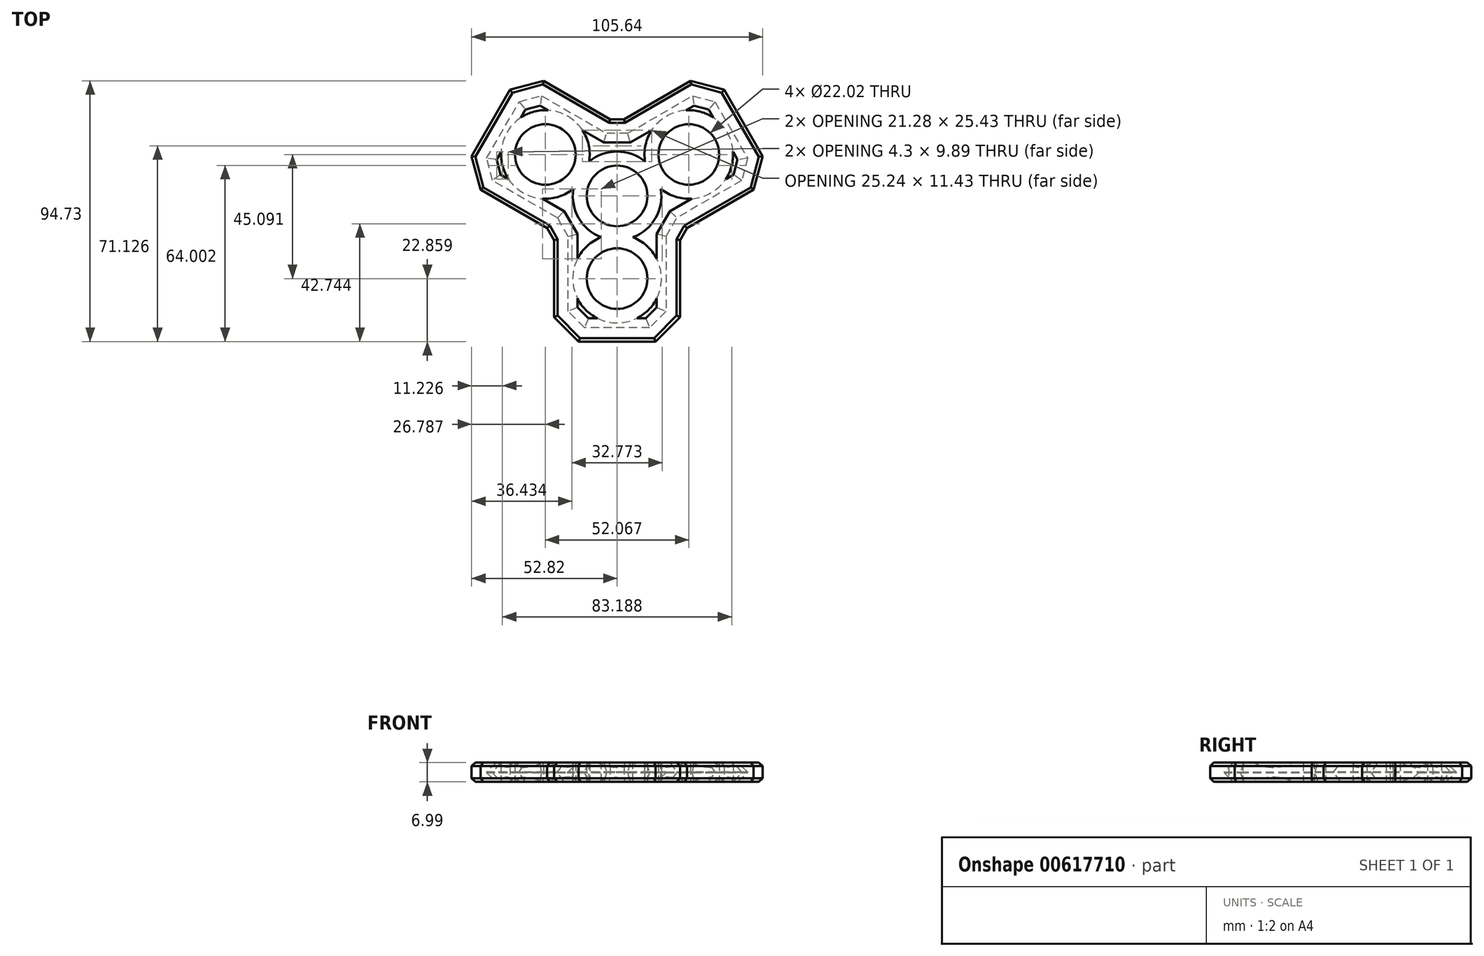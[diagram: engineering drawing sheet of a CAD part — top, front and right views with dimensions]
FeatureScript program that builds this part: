
annotation { "Feature Type Name" : "Feature", "Feature Type Description" : "" }
export const myFeature = defineFeature(function(context is Context, id is Id, definition is map)
    precondition{}
    {
        {
            var Q0;
            Q0=qCreatedBy(makeId("Top.planeOp"),FACE);
            var sketch = newSketch(context, id + "F0", { "sketchPlane" : qUnion([Q0])});
            skCircle(sketch, "E0", {"center": v(0, 0) * mm, "radius": 11.01 * mm});
            skCircle(sketch, "E1", {"center": v(0, 0) * mm, "radius": 19.05 * mm});
            skCircle(sketch, "E2", {"center": v(0, -30.06) * mm, "radius": 11.01 * mm});
            skLineSegment(sketch, "E3", {"start": v(0, 0) * mm, "end": v(0, -30.06) * mm});
            skCircle(sketch, "E4", {"center": v(0, -30.06) * mm, "radius": 19.05 * mm});
            skLineSegment(sketch, "E5", {"start": v(0, 0) * mm, "end": v(26.03, 15.03) * mm});
            skLineSegment(sketch, "E6", {"start": v(0, 0) * mm, "end": v(-26.03, 15.03) * mm});
            skCircle(sketch, "E7", {"center": v(-26.03, 15.03) * mm, "radius": 19.05 * mm});
            skCircle(sketch, "E8", {"center": v(26.03, 15.03) * mm, "radius": 19.05 * mm});
            skCircle(sketch, "E9", {"center": v(-26.03, 15.03) * mm, "radius": 11.01 * mm});
            skCircle(sketch, "E10", {"center": v(26.03, 15.03) * mm, "radius": 11.01 * mm});
            skLineSegment(sketch, "E11", {"start": v(-13.97, -52.92) * mm, "end": v(13.97, -52.92) * mm});
            skLineSegment(sketch, "E12", {"start": v(-22.86, -16.1) * mm, "end": v(-22.86, -44.03) * mm});
            skLineSegment(sketch, "E13", {"start": v(-22.86, -44.03) * mm, "end": v(-13.97, -52.92) * mm});
            skLineSegment(sketch, "E14", {"start": v(13.97, -52.92) * mm, "end": v(22.86, -44.03) * mm});
            skLineSegment(sketch, "E15", {"start": v(22.86, -44.03) * mm, "end": v(22.86, -16.1) * mm});
            skLineSegment(sketch, "E16", {"start": v(0, -30.06) * mm, "end": v(0, -52.92) * mm});
            skLineSegment(sketch, "E17", {"start": v(0, -30.06) * mm, "end": v(-22.86, -30.06) * mm});
            skLineSegment(sketch, "E18", {"start": v(0, -30.06) * mm, "end": v(22.86, -30.06) * mm});
            skLineSegment(sketch, "E19", {"start": v(18.42, -48.48) * mm, "end": v(0, -30.06) * mm});
            skLineSegment(sketch, "E20", {"start": v(-18.42, -48.48) * mm, "end": v(0, -30.06) * mm});
            skLineSegment(sketch, "E21.1.0", {"start": v(26.03, 15.03) * mm, "end": v(14.6, 34.83) * mm});
            skLineSegment(sketch, "E21.1.1", {"start": v(26.03, 15.03) * mm, "end": v(37.46, -4.77) * mm});
            skLineSegment(sketch, "E21.1.2", {"start": v(26.03, 15.03) * mm, "end": v(45.83, 26.46) * mm});
            skLineSegment(sketch, "E21.1.3", {"start": v(26.7, 41.81) * mm, "end": v(2.5, 27.84) * mm});
            skLineSegment(sketch, "E21.1.4", {"start": v(25.37, -11.75) * mm, "end": v(49.56, 2.22) * mm});
            skLineSegment(sketch, "E21.1.5", {"start": v(52.82, 14.36) * mm, "end": v(38.85, 38.56) * mm});
            skLineSegment(sketch, "E21.1.6", {"start": v(51.19, 8.3) * mm, "end": v(26.03, 15.03) * mm});
            skLineSegment(sketch, "E21.1.7", {"start": v(32.77, 40.19) * mm, "end": v(26.03, 15.03) * mm});
            skLineSegment(sketch, "E21.1.8", {"start": v(38.85, 38.56) * mm, "end": v(26.7, 41.81) * mm});
            skLineSegment(sketch, "E21.1.9", {"start": v(49.56, 2.22) * mm, "end": v(52.82, 14.36) * mm});
            skLineSegment(sketch, "E21.2.0", {"start": v(-26.03, 15.03) * mm, "end": v(-37.46, -4.77) * mm});
            skLineSegment(sketch, "E21.2.1", {"start": v(-26.03, 15.03) * mm, "end": v(-14.6, 34.83) * mm});
            skLineSegment(sketch, "E21.2.2", {"start": v(-26.03, 15.03) * mm, "end": v(-45.83, 26.46) * mm});
            skLineSegment(sketch, "E21.2.3", {"start": v(-49.56, 2.22) * mm, "end": v(-25.37, -11.75) * mm});
            skLineSegment(sketch, "E21.2.4", {"start": v(-2.5, 27.84) * mm, "end": v(-26.7, 41.81) * mm});
            skLineSegment(sketch, "E21.2.5", {"start": v(-38.85, 38.56) * mm, "end": v(-52.82, 14.36) * mm});
            skLineSegment(sketch, "E21.2.6", {"start": v(-32.77, 40.19) * mm, "end": v(-26.03, 15.03) * mm});
            skLineSegment(sketch, "E21.2.7", {"start": v(-51.19, 8.3) * mm, "end": v(-26.03, 15.03) * mm});
            skLineSegment(sketch, "E21.2.8", {"start": v(-52.82, 14.36) * mm, "end": v(-49.56, 2.22) * mm});
            skLineSegment(sketch, "E21.2.9", {"start": v(-26.7, 41.81) * mm, "end": v(-38.85, 38.56) * mm});
            skLineSegment(sketch, "E22", {"start": v(-22.86, -16.1) * mm, "end": v(-25.37, -11.75) * mm});
            skLineSegment(sketch, "E23", {"start": v(-2.5, 27.84) * mm, "end": v(2.5, 27.84) * mm});
            skLineSegment(sketch, "E24", {"start": v(25.37, -11.75) * mm, "end": v(22.86, -16.1) * mm});
            skSolve(sketch);
        }
        {
            var Q0;
            Q0 = qSketchRegion(id + "F0", true);
            var Q1;
            {var subQ0=sQuery(id+"F0.wireOp",EDGE,"E21.2.1");var subQ1=sQuery(id+"F0.wireOp",EDGE,"E7");var subQ2=makeQuery(id+"F0.imprint","INTERSECT",VERTEX,{"derivedFrom":[subQ1,subQ0]});Q1=makeQuery(id+"F0.imprint","IMPRINT",FACE,{"disambiguationData":[TD([[makeQuery(id+"F0.imprint","IMPRINT",EDGE,{"disambiguationData":[TD([[subQ2,-1.0]])],"derivedFrom":subQ1}),1.0]])]});}
            var Q2;
            {var subQ0=sQuery(id+"F0.wireOp",EDGE,"E21.2.6");var subQ1=sQuery(id+"F0.wireOp",EDGE,"E7");var subQ2=makeQuery(id+"F0.imprint","INTERSECT",VERTEX,{"derivedFrom":[subQ1,subQ0]});Q2=makeQuery(id+"F0.imprint","IMPRINT",FACE,{"disambiguationData":[TD([[makeQuery(id+"F0.imprint","IMPRINT",EDGE,{"disambiguationData":[TD([[subQ2,-1.0]])],"derivedFrom":subQ1}),1.0]])]});}
            var Q3;
            {var subQ0=sQuery(id+"F0.wireOp",EDGE,"E21.2.2");var subQ1=sQuery(id+"F0.wireOp",EDGE,"E7");var subQ2=makeQuery(id+"F0.imprint","INTERSECT",VERTEX,{"derivedFrom":[subQ1,subQ0]});Q3=makeQuery(id+"F0.imprint","IMPRINT",FACE,{"disambiguationData":[TD([[makeQuery(id+"F0.imprint","IMPRINT",EDGE,{"disambiguationData":[TD([[subQ2,-1.0]])],"derivedFrom":subQ1}),1.0]])]});}
            var Q4;
            {var subQ0=sQuery(id+"F0.wireOp",EDGE,"E21.2.7");var subQ1=sQuery(id+"F0.wireOp",EDGE,"E7");var subQ2=makeQuery(id+"F0.imprint","INTERSECT",VERTEX,{"derivedFrom":[subQ1,subQ0]});Q4=makeQuery(id+"F0.imprint","IMPRINT",FACE,{"disambiguationData":[TD([[makeQuery(id+"F0.imprint","IMPRINT",EDGE,{"disambiguationData":[TD([[subQ2,-1.0]])],"derivedFrom":subQ1}),1.0]])]});}
            var Q5;
            {var subQ0=sQuery(id+"F0.wireOp",EDGE,"E7");var subQ1=sQuery(id+"F0.wireOp",EDGE,"E1");var subQ2=makeQuery(id+"F0.imprint","INTERSECT",VERTEX,{"disambiguationData":[OD(1.0)],"derivedFrom":[subQ1,subQ0]});Q5=makeQuery(id+"F0.imprint","IMPRINT",FACE,{"disambiguationData":[TD([[makeQuery(id+"F0.imprint","IMPRINT",EDGE,{"disambiguationData":[TD([[subQ2,1.0]])],"derivedFrom":subQ0}),1.0]])]});}
            var Q6;
            {var subQ0=sQuery(id+"F0.wireOp",EDGE,"E7");var subQ1=sQuery(id+"F0.wireOp",EDGE,"E1");var subQ2=makeQuery(id+"F0.imprint","INTERSECT",VERTEX,{"disambiguationData":[OD(1.0)],"derivedFrom":[subQ1,subQ0]});Q6=makeQuery(id+"F0.imprint","IMPRINT",FACE,{"disambiguationData":[TD([[makeQuery(id+"F0.imprint","IMPRINT",EDGE,{"disambiguationData":[TD([[subQ2,1.0]])],"derivedFrom":subQ1}),1.0]])]});}
            var Q7;
            {var subQ0=sQuery(id+"F0.wireOp",EDGE,"E7");var subQ1=sQuery(id+"F0.wireOp",EDGE,"E1");var subQ2=makeQuery(id+"F0.imprint","INTERSECT",VERTEX,{"disambiguationData":[OD(0.0)],"derivedFrom":[subQ1,subQ0]});Q7=makeQuery(id+"F0.imprint","IMPRINT",FACE,{"disambiguationData":[TD([[makeQuery(id+"F0.imprint","IMPRINT",EDGE,{"disambiguationData":[TD([[subQ2,-1.0]])],"derivedFrom":subQ1}),1.0]])]});}
            var Q8;
            {var subQ0=sQuery(id+"F0.wireOp",EDGE,"E7");var subQ1=sQuery(id+"F0.wireOp",EDGE,"E1");var subQ2=makeQuery(id+"F0.imprint","INTERSECT",VERTEX,{"disambiguationData":[OD(0.0)],"derivedFrom":[subQ1,subQ0]});Q8=makeQuery(id+"F0.imprint","IMPRINT",FACE,{"disambiguationData":[TD([[makeQuery(id+"F0.imprint","IMPRINT",EDGE,{"disambiguationData":[TD([[subQ2,-1.0]])],"derivedFrom":subQ0}),1.0]])]});}
            var Q9;
            {var subQ3=sQuery(id+"F0.wireOp",EDGE,"E8");var subQ5=sQuery(id+"F0.wireOp",EDGE,"E1");var subQ6=makeQuery(id+"F0.imprint","INTERSECT",VERTEX,{"disambiguationData":[OD(0.0)],"derivedFrom":[subQ5,subQ3]});Q9=makeQuery(id+"F0.imprint","IMPRINT",FACE,{"disambiguationData":[TD([[makeQuery(id+"F0.imprint","IMPRINT",EDGE,{"disambiguationData":[TD([[subQ6,-1.0]])],"derivedFrom":subQ5}),1.0]])]});}
            var Q10;
            {var subQ0=sQuery(id+"F0.wireOp",EDGE,"E21.1.2");var subQ1=sQuery(id+"F0.wireOp",EDGE,"E8");var subQ2=makeQuery(id+"F0.imprint","INTERSECT",VERTEX,{"derivedFrom":[subQ1,subQ0]});Q10=makeQuery(id+"F0.imprint","IMPRINT",FACE,{"disambiguationData":[TD([[makeQuery(id+"F0.imprint","IMPRINT",EDGE,{"disambiguationData":[TD([[subQ2,1.0]])],"derivedFrom":subQ1}),1.0]])]});}
            var Q11;
            {var subQ0=sQuery(id+"F0.wireOp",EDGE,"E21.1.1");var subQ1=sQuery(id+"F0.wireOp",EDGE,"E8");var subQ2=makeQuery(id+"F0.imprint","INTERSECT",VERTEX,{"derivedFrom":[subQ1,subQ0]});Q11=makeQuery(id+"F0.imprint","IMPRINT",FACE,{"disambiguationData":[TD([[makeQuery(id+"F0.imprint","IMPRINT",EDGE,{"disambiguationData":[TD([[subQ2,-1.0]])],"derivedFrom":subQ1}),1.0]])]});}
            var Q12;
            {var subQ0=sQuery(id+"F0.wireOp",EDGE,"E8");var subQ1=sQuery(id+"F0.wireOp",EDGE,"E1");var subQ2=makeQuery(id+"F0.imprint","INTERSECT",VERTEX,{"disambiguationData":[OD(1.0)],"derivedFrom":[subQ1,subQ0]});Q12=makeQuery(id+"F0.imprint","IMPRINT",FACE,{"disambiguationData":[TD([[makeQuery(id+"F0.imprint","IMPRINT",EDGE,{"disambiguationData":[TD([[subQ2,-1.0]])],"derivedFrom":subQ0}),1.0]])]});}
            var Q13;
            {var subQ0=sQuery(id+"F0.wireOp",EDGE,"E8");var subQ1=sQuery(id+"F0.wireOp",EDGE,"E1");var subQ2=makeQuery(id+"F0.imprint","INTERSECT",VERTEX,{"disambiguationData":[OD(1.0)],"derivedFrom":[subQ1,subQ0]});Q13=makeQuery(id+"F0.imprint","IMPRINT",FACE,{"disambiguationData":[TD([[makeQuery(id+"F0.imprint","IMPRINT",EDGE,{"disambiguationData":[TD([[subQ2,-1.0]])],"derivedFrom":subQ1}),1.0]])]});}
            var Q14;
            {var subQ0=sQuery(id+"F0.wireOp",EDGE,"E8");var subQ1=sQuery(id+"F0.wireOp",EDGE,"E1");var subQ2=makeQuery(id+"F0.imprint","INTERSECT",VERTEX,{"disambiguationData":[OD(0.0)],"derivedFrom":[subQ1,subQ0]});Q14=makeQuery(id+"F0.imprint","IMPRINT",FACE,{"disambiguationData":[TD([[makeQuery(id+"F0.imprint","IMPRINT",EDGE,{"disambiguationData":[TD([[subQ2,1.0]])],"derivedFrom":subQ1}),1.0]])]});}
            var Q15;
            {var subQ3=sQuery(id+"F0.wireOp",EDGE,"E4");var subQ5=sQuery(id+"F0.wireOp",EDGE,"E1");var subQ6=makeQuery(id+"F0.imprint","INTERSECT",VERTEX,{"disambiguationData":[OD(1.0)],"derivedFrom":[subQ5,subQ3]});Q15=makeQuery(id+"F0.imprint","IMPRINT",FACE,{"disambiguationData":[TD([[makeQuery(id+"F0.imprint","IMPRINT",EDGE,{"disambiguationData":[TD([[subQ6,-1.0]])],"derivedFrom":subQ5}),1.0]])]});}
            var Q16;
            {var subQ0=sQuery(id+"F0.wireOp",EDGE,"E4");var subQ1=sQuery(id+"F0.wireOp",EDGE,"E1");var subQ2=makeQuery(id+"F0.imprint","INTERSECT",VERTEX,{"disambiguationData":[OD(0.0)],"derivedFrom":[subQ1,subQ0]});Q16=makeQuery(id+"F0.imprint","IMPRINT",FACE,{"disambiguationData":[TD([[makeQuery(id+"F0.imprint","IMPRINT",EDGE,{"disambiguationData":[TD([[subQ2,-1.0]])],"derivedFrom":subQ1}),1.0]])]});}
            var Q17;
            {var subQ0=sQuery(id+"F0.wireOp",EDGE,"E7");var subQ5=sQuery(id+"F0.wireOp",EDGE,"E1");var subQ6=makeQuery(id+"F0.imprint","INTERSECT",VERTEX,{"disambiguationData":[OD(1.0)],"derivedFrom":[subQ5,subQ0]});Q17=makeQuery(id+"F0.imprint","IMPRINT",FACE,{"disambiguationData":[TD([[makeQuery(id+"F0.imprint","IMPRINT",EDGE,{"disambiguationData":[TD([[subQ6,-1.0]])],"derivedFrom":subQ5}),1.0]])]});}
            var Q18;
            {var subQ0=sQuery(id+"F0.wireOp",EDGE,"E4");var subQ1=sQuery(id+"F0.wireOp",EDGE,"E1");var subQ2=makeQuery(id+"F0.imprint","INTERSECT",VERTEX,{"disambiguationData":[OD(1.0)],"derivedFrom":[subQ1,subQ0]});Q18=makeQuery(id+"F0.imprint","IMPRINT",FACE,{"disambiguationData":[TD([[makeQuery(id+"F0.imprint","IMPRINT",EDGE,{"disambiguationData":[TD([[subQ2,1.0]])],"derivedFrom":subQ1}),1.0]])]});}
            var Q19;
            {var subQ0=sQuery(id+"F0.wireOp",EDGE,"E4");var subQ1=sQuery(id+"F0.wireOp",EDGE,"E1");var subQ2=makeQuery(id+"F0.imprint","INTERSECT",VERTEX,{"disambiguationData":[OD(1.0)],"derivedFrom":[subQ1,subQ0]});Q19=makeQuery(id+"F0.imprint","IMPRINT",FACE,{"disambiguationData":[TD([[makeQuery(id+"F0.imprint","IMPRINT",EDGE,{"disambiguationData":[TD([[subQ2,1.0]])],"derivedFrom":subQ0}),1.0]])]});}
            var Q20;
            {var subQ0=sQuery(id+"F0.wireOp",EDGE,"E16");var subQ1=sQuery(id+"F0.wireOp",EDGE,"E2");var subQ2=makeQuery(id+"F0.imprint","INTERSECT",VERTEX,{"derivedFrom":[subQ1,subQ0]});Q20=makeQuery(id+"F0.imprint","IMPRINT",FACE,{"disambiguationData":[TD([[makeQuery(id+"F0.imprint","IMPRINT",EDGE,{"disambiguationData":[TD([[subQ2,-1.0]])],"derivedFrom":subQ1}),-1.0]])]});}
            var Q21;
            {var subQ0=sQuery(id+"F0.wireOp",EDGE,"E20");var subQ1=sQuery(id+"F0.wireOp",EDGE,"E2");var subQ2=makeQuery(id+"F0.imprint","INTERSECT",VERTEX,{"derivedFrom":[subQ1,subQ0]});Q21=makeQuery(id+"F0.imprint","IMPRINT",FACE,{"disambiguationData":[TD([[makeQuery(id+"F0.imprint","IMPRINT",EDGE,{"disambiguationData":[TD([[subQ2,-1.0]])],"derivedFrom":subQ1}),-1.0]])]});}
            var Q22;
            {var subQ0=sQuery(id+"F0.wireOp",EDGE,"E17");var subQ1=sQuery(id+"F0.wireOp",EDGE,"E2");var subQ2=makeQuery(id+"F0.imprint","INTERSECT",VERTEX,{"derivedFrom":[subQ1,subQ0]});Q22=makeQuery(id+"F0.imprint","IMPRINT",FACE,{"disambiguationData":[TD([[makeQuery(id+"F0.imprint","IMPRINT",EDGE,{"disambiguationData":[TD([[subQ2,-1.0]])],"derivedFrom":subQ1}),-1.0]])]});}
            var Q23;
            {var subQ0=sQuery(id+"F0.wireOp",EDGE,"E4");var subQ1=sQuery(id+"F0.wireOp",EDGE,"E1");var subQ2=makeQuery(id+"F0.imprint","INTERSECT",VERTEX,{"disambiguationData":[OD(0.0)],"derivedFrom":[subQ1,subQ0]});Q23=makeQuery(id+"F0.imprint","IMPRINT",FACE,{"disambiguationData":[TD([[makeQuery(id+"F0.imprint","IMPRINT",EDGE,{"disambiguationData":[TD([[subQ2,-1.0]])],"derivedFrom":subQ0}),1.0]])]});}
            var Q24;
            {var subQ0=sQuery(id+"F0.wireOp",EDGE,"E21.1.7");var subQ1=sQuery(id+"F0.wireOp",EDGE,"E8");var subQ2=makeQuery(id+"F0.imprint","INTERSECT",VERTEX,{"derivedFrom":[subQ1,subQ0]});Q24=makeQuery(id+"F0.imprint","IMPRINT",FACE,{"disambiguationData":[TD([[makeQuery(id+"F0.imprint","IMPRINT",EDGE,{"disambiguationData":[TD([[subQ2,1.0]])],"derivedFrom":subQ1}),1.0]])]});}
            var Q25;
            {var subQ0=sQuery(id+"F0.wireOp",EDGE,"E8");var subQ1=sQuery(id+"F0.wireOp",EDGE,"E1");var subQ2=makeQuery(id+"F0.imprint","INTERSECT",VERTEX,{"disambiguationData":[OD(0.0)],"derivedFrom":[subQ1,subQ0]});Q25=makeQuery(id+"F0.imprint","IMPRINT",FACE,{"disambiguationData":[TD([[makeQuery(id+"F0.imprint","IMPRINT",EDGE,{"disambiguationData":[TD([[subQ2,1.0]])],"derivedFrom":subQ0}),1.0]])]});}
            var Q26;
            {var subQ0=sQuery(id+"F0.wireOp",EDGE,"E21.1.7");var subQ1=sQuery(id+"F0.wireOp",EDGE,"E8");var subQ2=makeQuery(id+"F0.imprint","INTERSECT",VERTEX,{"derivedFrom":[subQ1,subQ0]});Q26=makeQuery(id+"F0.imprint","IMPRINT",FACE,{"disambiguationData":[TD([[makeQuery(id+"F0.imprint","IMPRINT",EDGE,{"disambiguationData":[TD([[subQ2,-1.0]])],"derivedFrom":subQ1}),1.0]])]});}
            var Q27;
            {var subQ0=sQuery(id+"F0.wireOp",EDGE,"E18");var subQ1=sQuery(id+"F0.wireOp",EDGE,"E2");var subQ2=makeQuery(id+"F0.imprint","INTERSECT",VERTEX,{"derivedFrom":[subQ1,subQ0]});Q27=makeQuery(id+"F0.imprint","IMPRINT",FACE,{"disambiguationData":[TD([[makeQuery(id+"F0.imprint","IMPRINT",EDGE,{"disambiguationData":[TD([[subQ2,1.0]])],"derivedFrom":subQ1}),-1.0]])]});}
            extrude(context, id + "F1", {"entities" : qUnion([Q0, Q1, Q2, Q3, Q4, Q5, Q6, Q7, Q8, Q9, Q10, Q11, Q12, Q13, Q14, Q15, Q16, Q17, Q18, Q19, Q20, Q21, Q22, Q23, Q24, Q25, Q26, Q27]), "depth" : 7 * mm, "offsetDistance" : 25.4 * mm});
        }
        {
            var Q0;
            Q0=makeQuery(id+"F1.opExtrude","CAP_EDGE",EDGE,{"disambiguationData":[OSD([sQuery(id+"F0.wireOp",EDGE,"E21.2.5")])],"isStart":false});
            var Q1;
            Q1=makeQuery(id+"F1.opExtrude","CAP_EDGE",EDGE,{"disambiguationData":[OSD([sQuery(id+"F0.wireOp",EDGE,"E21.2.4")])],"isStart":false});
            var Q2;
            Q2=makeQuery(id+"F1.opExtrude","CAP_EDGE",EDGE,{"disambiguationData":[OSD([sQuery(id+"F0.wireOp",EDGE,"E21.1.3")])],"isStart":false});
            var Q3;
            Q3=makeQuery(id+"F1.opExtrude","CAP_EDGE",EDGE,{"disambiguationData":[OSD([sQuery(id+"F0.wireOp",EDGE,"E21.1.5")])],"isStart":false});
            var Q4;
            Q4=makeQuery(id+"F1.opExtrude","CAP_EDGE",EDGE,{"disambiguationData":[OSD([sQuery(id+"F0.wireOp",EDGE,"E21.1.9")])],"isStart":false});
            var Q5;
            Q5=makeQuery(id+"F1.opExtrude","CAP_EDGE",EDGE,{"disambiguationData":[OSD([sQuery(id+"F0.wireOp",EDGE,"E21.1.4")])],"isStart":false});
            var Q6;
            Q6=makeQuery(id+"F1.opExtrude","CAP_EDGE",EDGE,{"disambiguationData":[OSD([sQuery(id+"F0.wireOp",EDGE,"E24")])],"isStart":false});
            var Q7;
            Q7=makeQuery(id+"F1.opExtrude","CAP_EDGE",EDGE,{"disambiguationData":[OSD([sQuery(id+"F0.wireOp",EDGE,"E15")])],"isStart":false});
            var Q8;
            Q8=makeQuery(id+"F1.opExtrude","CAP_EDGE",EDGE,{"disambiguationData":[OSD([sQuery(id+"F0.wireOp",EDGE,"E14")])],"isStart":false});
            var Q9;
            Q9=makeQuery(id+"F1.opExtrude","CAP_EDGE",EDGE,{"disambiguationData":[OSD([sQuery(id+"F0.wireOp",EDGE,"E11")])],"isStart":false});
            var Q10;
            Q10=makeQuery(id+"F1.opExtrude","CAP_EDGE",EDGE,{"disambiguationData":[OSD([sQuery(id+"F0.wireOp",EDGE,"E13")])],"isStart":false});
            var Q11;
            Q11=makeQuery(id+"F1.opExtrude","CAP_EDGE",EDGE,{"disambiguationData":[OSD([sQuery(id+"F0.wireOp",EDGE,"E12")])],"isStart":false});
            var Q12;
            Q12=makeQuery(id+"F1.opExtrude","CAP_EDGE",EDGE,{"disambiguationData":[OSD([sQuery(id+"F0.wireOp",EDGE,"E22")])],"isStart":false});
            var Q13;
            Q13=makeQuery(id+"F1.opExtrude","CAP_EDGE",EDGE,{"disambiguationData":[OSD([sQuery(id+"F0.wireOp",EDGE,"E21.2.3")])],"isStart":false});
            var Q14;
            Q14=makeQuery(id+"F1.opExtrude","CAP_EDGE",EDGE,{"disambiguationData":[OSD([sQuery(id+"F0.wireOp",EDGE,"E21.2.8")])],"isStart":false});
            var Q15;
            Q15=makeQuery(id+"F1.opExtrude","CAP_EDGE",EDGE,{"disambiguationData":[OSD([sQuery(id+"F0.wireOp",EDGE,"E21.2.9")])],"isStart":false});
            var Q16;
            Q16=makeQuery(id+"F1.opExtrude","CAP_EDGE",EDGE,{"disambiguationData":[OSD([sQuery(id+"F0.wireOp",EDGE,"E23")])],"isStart":false});
            var Q17;
            Q17=makeQuery(id+"F1.opExtrude","CAP_EDGE",EDGE,{"disambiguationData":[OSD([sQuery(id+"F0.wireOp",EDGE,"E21.1.8")])],"isStart":false});
            chamfer(context, id + "F2", {"entities" : qUnion([Q0, Q1, Q2, Q3, Q4, Q5, Q6, Q7, Q8, Q9, Q10, Q11, Q12, Q13, Q14, Q15, Q16, Q17]), "width" : 1.27 * mm, "tangentPropagation" : true});
        }
        {
            var Q0;
            Q0=makeQuery(id+"F1.opExtrude","CAP_EDGE",EDGE,{"disambiguationData":[OSD([sQuery(id+"F0.wireOp",EDGE,"E21.1.5")])],"isStart":true});
            var Q1;
            Q1=makeQuery(id+"F1.opExtrude","CAP_EDGE",EDGE,{"disambiguationData":[OSD([sQuery(id+"F0.wireOp",EDGE,"E21.1.8")])],"isStart":true});
            var Q2;
            Q2=makeQuery(id+"F1.opExtrude","CAP_EDGE",EDGE,{"disambiguationData":[OSD([sQuery(id+"F0.wireOp",EDGE,"E21.1.3")])],"isStart":true});
            var Q3;
            Q3=makeQuery(id+"F1.opExtrude","CAP_EDGE",EDGE,{"disambiguationData":[OSD([sQuery(id+"F0.wireOp",EDGE,"E21.1.9")])],"isStart":true});
            var Q4;
            Q4=makeQuery(id+"F1.opExtrude","CAP_EDGE",EDGE,{"disambiguationData":[OSD([sQuery(id+"F0.wireOp",EDGE,"E21.1.4")])],"isStart":true});
            var Q5;
            Q5=makeQuery(id+"F1.opExtrude","CAP_EDGE",EDGE,{"disambiguationData":[OSD([sQuery(id+"F0.wireOp",EDGE,"E24")])],"isStart":true});
            var Q6;
            Q6=makeQuery(id+"F1.opExtrude","CAP_EDGE",EDGE,{"disambiguationData":[OSD([sQuery(id+"F0.wireOp",EDGE,"E23")])],"isStart":true});
            var Q7;
            Q7=makeQuery(id+"F1.opExtrude","CAP_EDGE",EDGE,{"disambiguationData":[OSD([sQuery(id+"F0.wireOp",EDGE,"E21.2.4")])],"isStart":true});
            var Q8;
            Q8=makeQuery(id+"F1.opExtrude","CAP_EDGE",EDGE,{"disambiguationData":[OSD([sQuery(id+"F0.wireOp",EDGE,"E21.2.9")])],"isStart":true});
            var Q9;
            Q9=makeQuery(id+"F1.opExtrude","CAP_EDGE",EDGE,{"disambiguationData":[OSD([sQuery(id+"F0.wireOp",EDGE,"E21.2.5")])],"isStart":true});
            var Q10;
            Q10=makeQuery(id+"F1.opExtrude","CAP_EDGE",EDGE,{"disambiguationData":[OSD([sQuery(id+"F0.wireOp",EDGE,"E21.2.8")])],"isStart":true});
            var Q11;
            Q11=makeQuery(id+"F1.opExtrude","CAP_EDGE",EDGE,{"disambiguationData":[OSD([sQuery(id+"F0.wireOp",EDGE,"E21.2.3")])],"isStart":true});
            var Q12;
            Q12=makeQuery(id+"F1.opExtrude","CAP_EDGE",EDGE,{"disambiguationData":[OSD([sQuery(id+"F0.wireOp",EDGE,"E22")])],"isStart":true});
            var Q13;
            Q13=makeQuery(id+"F1.opExtrude","CAP_EDGE",EDGE,{"disambiguationData":[OSD([sQuery(id+"F0.wireOp",EDGE,"E12")])],"isStart":true});
            var Q14;
            Q14=makeQuery(id+"F1.opExtrude","CAP_EDGE",EDGE,{"disambiguationData":[OSD([sQuery(id+"F0.wireOp",EDGE,"E13")])],"isStart":true});
            var Q15;
            Q15=makeQuery(id+"F1.opExtrude","CAP_EDGE",EDGE,{"disambiguationData":[OSD([sQuery(id+"F0.wireOp",EDGE,"E11")])],"isStart":true});
            var Q16;
            Q16=makeQuery(id+"F1.opExtrude","CAP_EDGE",EDGE,{"disambiguationData":[OSD([sQuery(id+"F0.wireOp",EDGE,"E14")])],"isStart":true});
            var Q17;
            Q17=makeQuery(id+"F1.opExtrude","CAP_EDGE",EDGE,{"disambiguationData":[OSD([sQuery(id+"F0.wireOp",EDGE,"E15")])],"isStart":true});
            chamfer(context, id + "F3", {"entities" : qUnion([Q0, Q1, Q2, Q3, Q4, Q5, Q6, Q7, Q8, Q9, Q10, Q11, Q12, Q13, Q14, Q15, Q16, Q17]), "width" : 1.27 * mm, "tangentPropagation" : true});
        }
        {
            var Q0;
            Q0=makeQuery(id+"F1.opExtrude","CAP_FACE",FACE,{"disambiguationData":[OSD([sQuery(id+"F0.wireOp",EDGE,"E0"),sQuery(id+"F0.wireOp",EDGE,"E2"),sQuery(id+"F0.wireOp",EDGE,"E9"),sQuery(id+"F0.wireOp",EDGE,"E10"),sQuery(id+"F0.wireOp",EDGE,"E11"),sQuery(id+"F0.wireOp",EDGE,"E12"),sQuery(id+"F0.wireOp",EDGE,"E13"),sQuery(id+"F0.wireOp",EDGE,"E14"),sQuery(id+"F0.wireOp",EDGE,"E15"),sQuery(id+"F0.wireOp",EDGE,"E21.1.3"),sQuery(id+"F0.wireOp",EDGE,"E21.1.4"),sQuery(id+"F0.wireOp",EDGE,"E21.1.5"),sQuery(id+"F0.wireOp",EDGE,"E21.1.8"),sQuery(id+"F0.wireOp",EDGE,"E21.1.9"),sQuery(id+"F0.wireOp",EDGE,"E21.2.3"),sQuery(id+"F0.wireOp",EDGE,"E21.2.4"),sQuery(id+"F0.wireOp",EDGE,"E21.2.5"),sQuery(id+"F0.wireOp",EDGE,"E21.2.8"),sQuery(id+"F0.wireOp",EDGE,"E21.2.9"),sQuery(id+"F0.wireOp",EDGE,"E22"),sQuery(id+"F0.wireOp",EDGE,"E23"),sQuery(id+"F0.wireOp",EDGE,"E24")])],"isStart":true});
            var Q1;
            Q1=makeQuery(id+"F1.opExtrude","CAP_FACE",FACE,{"disambiguationData":[OSD([sQuery(id+"F0.wireOp",EDGE,"E0"),sQuery(id+"F0.wireOp",EDGE,"E2"),sQuery(id+"F0.wireOp",EDGE,"E9"),sQuery(id+"F0.wireOp",EDGE,"E10"),sQuery(id+"F0.wireOp",EDGE,"E11"),sQuery(id+"F0.wireOp",EDGE,"E12"),sQuery(id+"F0.wireOp",EDGE,"E13"),sQuery(id+"F0.wireOp",EDGE,"E14"),sQuery(id+"F0.wireOp",EDGE,"E15"),sQuery(id+"F0.wireOp",EDGE,"E21.1.3"),sQuery(id+"F0.wireOp",EDGE,"E21.1.4"),sQuery(id+"F0.wireOp",EDGE,"E21.1.5"),sQuery(id+"F0.wireOp",EDGE,"E21.1.8"),sQuery(id+"F0.wireOp",EDGE,"E21.1.9"),sQuery(id+"F0.wireOp",EDGE,"E21.2.3"),sQuery(id+"F0.wireOp",EDGE,"E21.2.4"),sQuery(id+"F0.wireOp",EDGE,"E21.2.5"),sQuery(id+"F0.wireOp",EDGE,"E21.2.8"),sQuery(id+"F0.wireOp",EDGE,"E21.2.9"),sQuery(id+"F0.wireOp",EDGE,"E22"),sQuery(id+"F0.wireOp",EDGE,"E23"),sQuery(id+"F0.wireOp",EDGE,"E24")])],"isStart":false});
            shell(context, id + "F4", {"entities" : qUnion([Q0, Q1]), "thickness" : 5.08 * mm});
        }
    });
